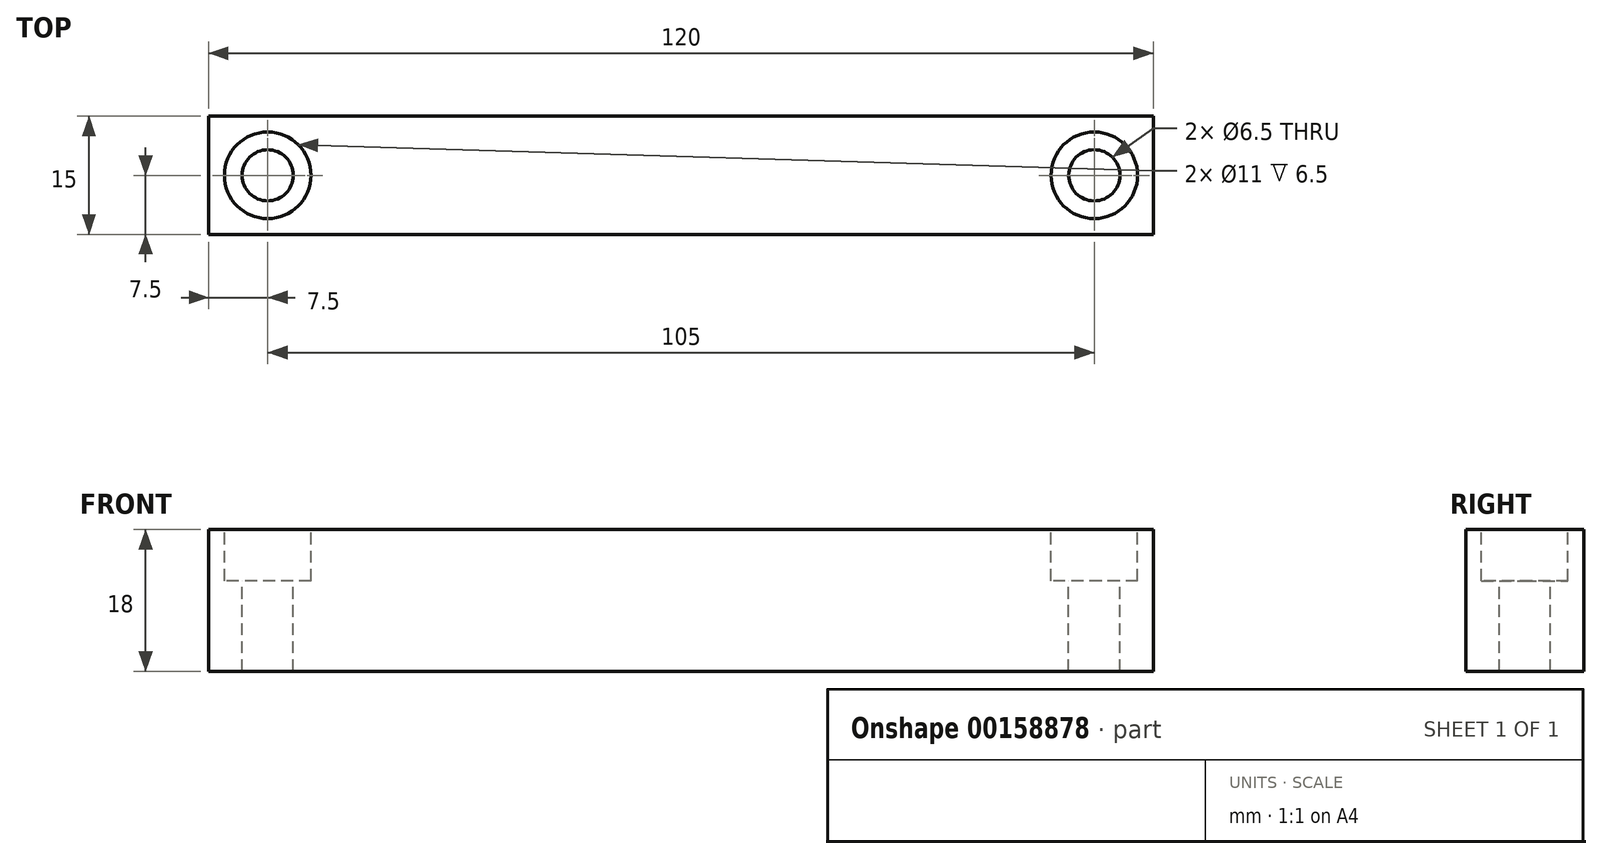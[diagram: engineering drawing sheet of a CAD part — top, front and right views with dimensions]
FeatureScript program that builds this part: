
annotation { "Feature Type Name" : "Feature", "Feature Type Description" : "" }
export const myFeature = defineFeature(function(context is Context, id is Id, definition is map)
    precondition{}
    {
        {
            var Q0;
            Q0=qCreatedBy(makeId("Front.planeOp"),FACE);
            var sketch = newSketch(context, id + "F0", { "sketchPlane" : qUnion([Q0])});
            skLineSegment(sketch, "E0", {"start": v(0, 0) * mm, "end": v(0, 61.5) * mm});
            skLineSegment(sketch, "E1", {"start": v(0, 0) * mm, "end": v(90, 0) * mm});
            skLineSegment(sketch, "E2", {"start": v(90, 0) * mm, "end": v(90, 61.5) * mm});
            skLineSegment(sketch, "E3.0", {"start": v(-15, -15) * mm, "end": v(-15, 61.5) * mm});
            skLineSegment(sketch, "E3.1", {"start": v(-15, -15) * mm, "end": v(105, -15) * mm});
            skLineSegment(sketch, "E3.2", {"start": v(105, -15) * mm, "end": v(105, 61.5) * mm});
            skLineSegment(sketch, "E4", {"start": v(-15, 61.5) * mm, "end": v(0, 61.5) * mm});
            skLineSegment(sketch, "E5", {"start": v(90, 61.5) * mm, "end": v(105, 61.5) * mm});
            skSolve(sketch);
        }
        {
            var Q0;
            Q0=qSketchRegion(id+"F0",true);
            extrude(context, id + "F1", {"entities" : qUnion([Q0]), "depth" : 15 * mm});
        }
        {
            var Q0;
            Q0=makeQuery(id+"F1.opExtrude","CAP_FACE",FACE,{"disambiguationData":[OSD([sQuery(id+"F0.wireOp",EDGE,"E0"),sQuery(id+"F0.wireOp",EDGE,"E1"),sQuery(id+"F0.wireOp",EDGE,"E2"),sQuery(id+"F0.wireOp",EDGE,"E3.0"),sQuery(id+"F0.wireOp",EDGE,"E3.1"),sQuery(id+"F0.wireOp",EDGE,"E3.2"),sQuery(id+"F0.wireOp",EDGE,"E4"),sQuery(id+"F0.wireOp",EDGE,"E5")])],"isStart":false});
            var sketch = newSketch(context, id + "F2", { "sketchPlane" : qUnion([Q0])});
            skLineSegment(sketch, "E6.bottom", {"start": v(8, -15) * mm, "end": v(82, -15) * mm});
            skLineSegment(sketch, "E6.top", {"start": v(8, -20) * mm, "end": v(82, -20) * mm});
            skLineSegment(sketch, "E6.left", {"start": v(8, -15) * mm, "end": v(8, -20) * mm});
            skLineSegment(sketch, "E6.right", {"start": v(82, -15) * mm, "end": v(82, -20) * mm});
            skSolve(sketch);
        }
        {
            var Q0;
            Q0=qSketchRegion(id+"F2",true);
            var Q1;
            Q1=makeQuery(id+"F1.opExtrude","CAP_FACE",FACE,{"disambiguationData":[OSD([sQuery(id+"F0.wireOp",EDGE,"E0"),sQuery(id+"F0.wireOp",EDGE,"E1"),sQuery(id+"F0.wireOp",EDGE,"E2"),sQuery(id+"F0.wireOp",EDGE,"E3.0"),sQuery(id+"F0.wireOp",EDGE,"E3.1"),sQuery(id+"F0.wireOp",EDGE,"E3.2"),sQuery(id+"F0.wireOp",EDGE,"E4"),sQuery(id+"F0.wireOp",EDGE,"E5")])],"isStart":true});
            extrude(context, id + "F3", {"entities" : qUnion([Q0]), "operationType" : NewBodyOperationType.ADD, "endBound" : BoundingType.UP_TO_SURFACE, "oppositeDirection" : true, "endBoundEntityFace" : qUnion([Q1]), "depth" : 25 * mm});
        }
        {
            var Q0;
            Q0=makeQuery(id+"F1.opExtrude","SWEPT_EDGE",EDGE,{"disambiguationData":[OSD([sQuery(id+"F0.wireOp",EDGE,"E0"),sQuery(id+"F0.wireOp",EDGE,"E1")])]});
            var Q1;
            Q1=makeQuery(id+"F1.opExtrude","SWEPT_EDGE",EDGE,{"disambiguationData":[OSD([sQuery(id+"F0.wireOp",EDGE,"E1"),sQuery(id+"F0.wireOp",EDGE,"E2")])]});
            var Q2;
            Q2=makeQuery(id+"F3.opExtrude","SWEPT_EDGE",EDGE,{"disambiguationData":[OSD([sQuery(id+"F0.wireOp",EDGE,"E3.1"),sQuery(id+"F2.wireOp",EDGE,"E6.bottom"),sQuery(id+"F2.wireOp",EDGE,"E6.left")])]});
            var Q3;
            Q3=makeQuery(id+"F3.opExtrude","SWEPT_EDGE",EDGE,{"disambiguationData":[OSD([sQuery(id+"F0.wireOp",EDGE,"E3.1"),sQuery(id+"F2.wireOp",EDGE,"E6.bottom"),sQuery(id+"F2.wireOp",EDGE,"E6.right")])]});
            fillet(context, id + "F4", {"entities" : qUnion([Q0, Q1, Q2, Q3]), "radius" : 5 * mm, "tangentPropagation" : true, "allowEdgeOverflow" : false});
        }
        {
            var Q0;
            Q0=makeQuery(id+"F1.opExtrude","SWEPT_EDGE",EDGE,{"disambiguationData":[OSD([sQuery(id+"F0.wireOp",EDGE,"E3.0"),sQuery(id+"F0.wireOp",EDGE,"E3.1")])]});
            var Q1;
            Q1=makeQuery(id+"F1.opExtrude","SWEPT_EDGE",EDGE,{"disambiguationData":[OSD([sQuery(id+"F0.wireOp",EDGE,"E3.1"),sQuery(id+"F0.wireOp",EDGE,"E3.2")])]});
            fillet(context, id + "F5", {"entities" : qUnion([Q0, Q1]), "radius" : 8 * mm, "tangentPropagation" : true, "allowEdgeOverflow" : false});
        }
        {
            var Q0;
            Q0=makeQuery(id+"F4.opFillet","BLEND_EDGE",EDGE,{"blendedFrom":[makeQuery(id+"F3.opExtrude","SWEPT_EDGE",EDGE,{"disambiguationData":[OSD([sQuery(id+"F0.wireOp",EDGE,"E3.1"),sQuery(id+"F2.wireOp",EDGE,"E6.bottom"),sQuery(id+"F2.wireOp",EDGE,"E6.right")])]}),makeQuery(id+"F3.opExtrude","SWEPT_FACE",FACE,{"disambiguationData":[OSD([sQuery(id+"F2.wireOp",EDGE,"E6.top")])]})],"blendedInto":[makeQuery(id+"F3.opExtrude","SWEPT_FACE",FACE,{"disambiguationData":[OSD([sQuery(id+"F2.wireOp",EDGE,"E6.top")])]})]});
            var Q1;
            Q1=makeQuery(id+"F4.opFillet","BLEND_EDGE",EDGE,{"blendedFrom":[makeQuery(id+"F3.opExtrude","SWEPT_EDGE",EDGE,{"disambiguationData":[OSD([sQuery(id+"F0.wireOp",EDGE,"E3.1"),sQuery(id+"F2.wireOp",EDGE,"E6.bottom"),sQuery(id+"F2.wireOp",EDGE,"E6.left")])]}),makeQuery(id+"F3.opExtrude","SWEPT_FACE",FACE,{"disambiguationData":[OSD([sQuery(id+"F2.wireOp",EDGE,"E6.top")])]})],"blendedInto":[makeQuery(id+"F3.opExtrude","SWEPT_FACE",FACE,{"disambiguationData":[OSD([sQuery(id+"F2.wireOp",EDGE,"E6.top")])]})]});
            fillet(context, id + "F6", {"entities" : qUnion([Q0, Q1]), "radius" : 5 * mm, "tangentPropagation" : true, "allowEdgeOverflow" : false});
        }
        {
            var Q0;
            Q0=makeQuery(id+"F3.boolean.opBoolean","MERGE",FACE,{"derivedFrom":[makeQuery(id+"F1.opExtrude","CAP_FACE",FACE,{"disambiguationData":[OSD([sQuery(id+"F0.wireOp",EDGE,"E0"),sQuery(id+"F0.wireOp",EDGE,"E1"),sQuery(id+"F0.wireOp",EDGE,"E2"),sQuery(id+"F0.wireOp",EDGE,"E3.0"),sQuery(id+"F0.wireOp",EDGE,"E3.1"),sQuery(id+"F0.wireOp",EDGE,"E3.2"),sQuery(id+"F0.wireOp",EDGE,"E4"),sQuery(id+"F0.wireOp",EDGE,"E5")])],"isStart":false}),makeQuery(id+"F3.opExtrude","CAP_FACE",FACE,{"disambiguationData":[OSD([sQuery(id+"F2.wireOp",EDGE,"E6.bottom"),sQuery(id+"F2.wireOp",EDGE,"E6.top"),sQuery(id+"F2.wireOp",EDGE,"E6.left"),sQuery(id+"F2.wireOp",EDGE,"E6.right")])],"isStart":true})]});
            var sketch = newSketch(context, id + "F7", { "sketchPlane" : qUnion([Q0])});
            skCircle(sketch, "E7", {"center": v(19.6, -10) * mm, "radius": 3.5 * mm});
            skCircle(sketch, "E8", {"center": v(70.4, -10) * mm, "radius": 3.5 * mm});
            skLineSegment(sketch, "E9", {"start": v(19.6, -10) * mm, "end": v(70.4, -10) * mm, "construction": true});
            skLineSegment(sketch, "E10", {"start": v(45, -10) * mm, "end": v(45, 0) * mm, "construction": true});
            skSolve(sketch);
        }
        {
            var Q0;
            Q0=sQuery(id+"F7.wireOp",VERTEX,"E7.center");
            var Q1;
            Q1=sQuery(id+"F7.wireOp",VERTEX,"E9.end");
            var Q2;
            Q2=makeQuery(id+"F1.opExtrude","SWEPT_BODY",BODY,{"disambiguationData":[OSD([sQuery(id+"F0.wireOp",EDGE,"E0"),sQuery(id+"F0.wireOp",EDGE,"E1"),sQuery(id+"F0.wireOp",EDGE,"E2"),sQuery(id+"F0.wireOp",EDGE,"E3.0"),sQuery(id+"F0.wireOp",EDGE,"E3.1"),sQuery(id+"F0.wireOp",EDGE,"E3.2"),sQuery(id+"F0.wireOp",EDGE,"E4"),sQuery(id+"F0.wireOp",EDGE,"E5")])]});
            hole(context, id + "F8", {"style" : HoleStyle.SIMPLE, "endStyle" : HoleEndStyle.THROUGH, "holeDiameter" : 7 * mm, "locations" : qUnion([Q0, Q1]), "scope" : qUnion([Q2]), "isTappedThrough" : true});
        }
        {
            var Q0;
            Q0=makeQuery(id+"F1.opExtrude","SWEPT_FACE",FACE,{"disambiguationData":[OSD([sQuery(id+"F0.wireOp",EDGE,"E4")])]});
            var sketch = newSketch(context, id + "F9", { "sketchPlane" : qUnion([Q0])});
            skLineSegment(sketch, "E11", {"start": v(-15, -7.5) * mm, "end": v(0, -7.5) * mm, "construction": true});
            skLineSegment(sketch, "E12", {"start": v(0, -7.5) * mm, "end": v(-7.5, -15) * mm, "construction": true});
            skLineSegment(sketch, "E13", {"start": v(-7.5, -15) * mm, "end": v(-7.5, -7.5) * mm, "construction": true});
            skSolve(sketch);
        }
        {
            var Q0;
            Q0=makeQuery(id+"F1.opExtrude","SWEPT_FACE",FACE,{"disambiguationData":[OSD([sQuery(id+"F0.wireOp",EDGE,"E5")])]});
            var sketch = newSketch(context, id + "F10", { "sketchPlane" : qUnion([Q0])});
            skLineSegment(sketch, "E14", {"start": v(105, -7.5) * mm, "end": v(90, -7.5) * mm, "construction": true});
            skLineSegment(sketch, "E15", {"start": v(97.5, 0) * mm, "end": v(97.5, -7.5) * mm, "construction": true});
            skSolve(sketch);
        }
        {
            var Q0;
            Q0=sQuery(id+"F9.wireOp",VERTEX,"E13.end");
            var Q1;
            Q1=sQuery(id+"F10.wireOp",VERTEX,"E15.end");
            var Q2;
            Q2=makeQuery(id+"F1.opExtrude","SWEPT_BODY",BODY,{"disambiguationData":[OSD([sQuery(id+"F0.wireOp",EDGE,"E0"),sQuery(id+"F0.wireOp",EDGE,"E1"),sQuery(id+"F0.wireOp",EDGE,"E2"),sQuery(id+"F0.wireOp",EDGE,"E3.0"),sQuery(id+"F0.wireOp",EDGE,"E3.1"),sQuery(id+"F0.wireOp",EDGE,"E3.2"),sQuery(id+"F0.wireOp",EDGE,"E4"),sQuery(id+"F0.wireOp",EDGE,"E5")])]});
            hole(context, id + "F11", {"style" : HoleStyle.SIMPLE, "endStyle" : HoleEndStyle.BLIND, "holeDiameter" : 5 * mm, "holeDepth" : 20 * mm, "locations" : qUnion([Q0, Q1]), "scope" : qUnion([Q2])});
        }
        {
            var Q0;
            Q0=makeQuery(id+"F1.opExtrude","SWEPT_FACE",FACE,{"disambiguationData":[OSD([sQuery(id+"F0.wireOp",EDGE,"E4")])]});
            var sketch = newSketch(context, id + "F12", { "sketchPlane" : qUnion([Q0])});
            skLineSegment(sketch, "E16.bottom", {"start": v(-15, 0) * mm, "end": v(105, 0) * mm});
            skLineSegment(sketch, "E16.top", {"start": v(-15, -15) * mm, "end": v(105, -15) * mm});
            skLineSegment(sketch, "E16.left", {"start": v(-15, 0) * mm, "end": v(-15, -15) * mm});
            skLineSegment(sketch, "E16.right", {"start": v(105, 0) * mm, "end": v(105, -15) * mm});
            skSolve(sketch);
        }
        {
            var Q0;
            {var subQ2=sQuery(id+"F12.wireOp",EDGE,"E16.right");Q0=makeQuery(id+"F12.imprint","IMPRINT",FACE,{"disambiguationData":[TD([[makeQuery(id+"F12.imprint","IMPRINT",EDGE,{"derivedFrom":subQ2}),-1.0]])]});}
            var Q1;
            {var subQ1=sQuery(id+"F12.wireOp",EDGE,"E16.left");Q1=makeQuery(id+"F12.imprint","IMPRINT",FACE,{"disambiguationData":[TD([[makeQuery(id+"F12.imprint","IMPRINT",EDGE,{"derivedFrom":subQ1}),-1.0]])]});}
            extrude(context, id + "F13", {"entities" : qUnion([Q0, Q1]), "depth" : 18 * mm});
        }
        {
            var Q0;
            Q0=makeQuery(id+"F1.opExtrude","SWEPT_BODY",BODY,{"disambiguationData":[OSD([sQuery(id+"F0.wireOp",EDGE,"E0"),sQuery(id+"F0.wireOp",EDGE,"E1"),sQuery(id+"F0.wireOp",EDGE,"E2"),sQuery(id+"F0.wireOp",EDGE,"E3.0"),sQuery(id+"F0.wireOp",EDGE,"E3.1"),sQuery(id+"F0.wireOp",EDGE,"E3.2"),sQuery(id+"F0.wireOp",EDGE,"E4"),sQuery(id+"F0.wireOp",EDGE,"E5")])]});
            deleteBodies(context, id + "F14", {"entities" : qUnion([Q0])});
        }
        {
            var Q0;
            Q0=makeQuery(id+"F13.opExtrude","CAP_FACE",FACE,{"disambiguationData":[OSD([sQuery(id+"F11.hole-0.sketch.wireOp",EDGE,"core_line_2"),sQuery(id+"F11.hole-0.sketch.wireOp",EDGE,"core_line_3"),sQuery(id+"F12.wireOp",EDGE,"E16.bottom"),sQuery(id+"F12.wireOp",EDGE,"E16.top"),sQuery(id+"F12.wireOp",EDGE,"E16.left"),sQuery(id+"F12.wireOp",EDGE,"E16.right")])],"isStart":false});
            var sketch = newSketch(context, id + "F15", { "sketchPlane" : qUnion([Q0])});
            skLineSegment(sketch, "E17", {"start": v(-7.5, -7.5) * mm, "end": v(97.5, -7.5) * mm, "construction": true});
            skSolve(sketch);
        }
        {
            var Q0;
            Q0=sQuery(id+"F15.wireOp",VERTEX,"E17.start");
            var Q1;
            Q1=sQuery(id+"F15.wireOp",VERTEX,"E17.end");
            var Q2;
            Q2=makeQuery(id+"F13.opExtrude","SWEPT_BODY",BODY,{"disambiguationData":[OSD([sQuery(id+"F11.hole-0.sketch.wireOp",EDGE,"core_line_2"),sQuery(id+"F11.hole-0.sketch.wireOp",EDGE,"core_line_3"),sQuery(id+"F12.wireOp",EDGE,"E16.bottom"),sQuery(id+"F12.wireOp",EDGE,"E16.top"),sQuery(id+"F12.wireOp",EDGE,"E16.left"),sQuery(id+"F12.wireOp",EDGE,"E16.right")])]});
            hole(context, id + "F16", {"style" : HoleStyle.C_BORE, "endStyle" : HoleEndStyle.THROUGH, "holeDiameter" : 6.5 * mm, "cBoreDiameter" : 11 * mm, "cBoreDepth" : 6.5 * mm, "locations" : qUnion([Q0, Q1]), "scope" : qUnion([Q2]), "isTappedThrough" : true});
        }
    });
